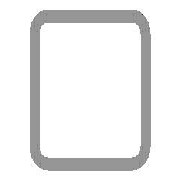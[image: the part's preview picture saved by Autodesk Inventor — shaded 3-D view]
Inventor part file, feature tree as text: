
AUTODESK INVENTOR PART (.ipt)
format: ipt  version: 2025.1 (Build 291241020, 241B)  size: 138,752 bytes
history: native  units: mm (DEFAULTED — no unit token found)
features: other x3, sketch x1, plane x1
ambient origin geometry x8: Origin, YZ Plane, XZ Plane, XY Plane, X Axis, Y Axis, Z Axis, Center Point
bodies: Solid1 (feature_tree), Body (feature_tree)
feature tree (5):
  other  "Driven Length"
  other  "Start plane"
  other  "End plane"
  sketch  "Sketch3"  dims[d3=2750.0mm d4=0.0mm d7=6.0mm d10=100.0mm d11=100.0mm d12=4.0mm d13=-0.0mm d14=2750.0mm d15=50.0mm d16=50.0mm d17=90.0deg d18=2750.0mm d19=4.0mm d20=4.0mm]
  plane  "Work Plane3"
